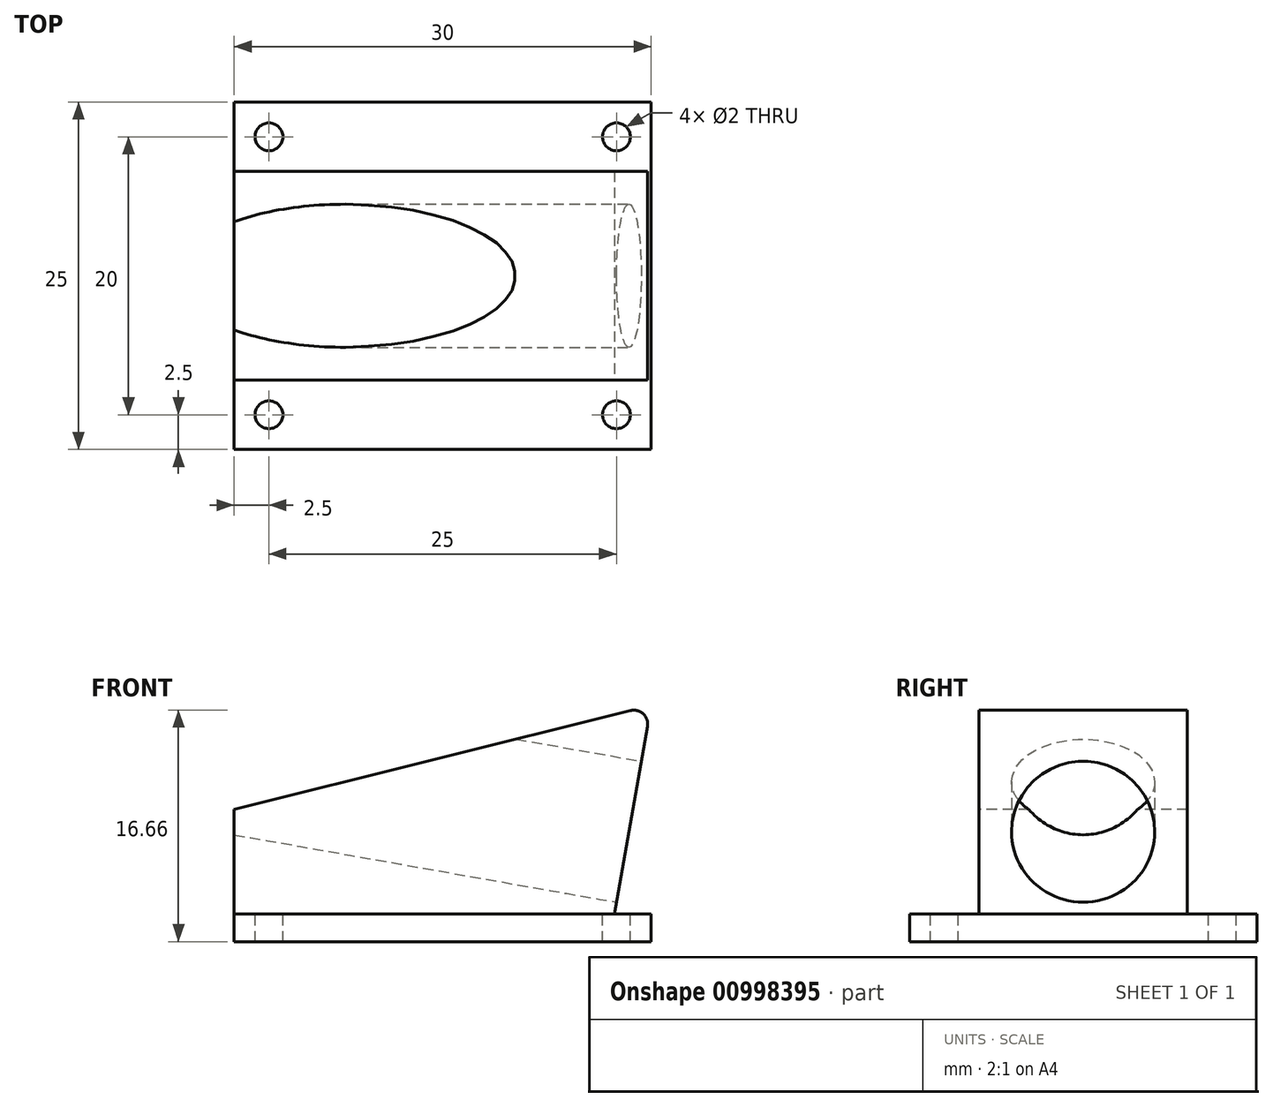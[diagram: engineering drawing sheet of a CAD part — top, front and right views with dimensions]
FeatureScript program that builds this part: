
annotation { "Feature Type Name" : "Feature", "Feature Type Description" : "" }
export const myFeature = defineFeature(function(context is Context, id is Id, definition is map)
    precondition{}
    {
        {
            var Q0;
            Q0=qCreatedBy(makeId("Top.planeOp"),FACE);
            var sketch = newSketch(context, id + "F0", { "sketchPlane" : qUnion([Q0])});
            skLineSegment(sketch, "E0.bottom", {"start": v(-15, 12.5) * mm, "end": v(15, 12.5) * mm});
            skLineSegment(sketch, "E0.top", {"start": v(-15, -12.5) * mm, "end": v(15, -12.5) * mm});
            skLineSegment(sketch, "E0.left", {"start": v(-15, 12.5) * mm, "end": v(-15, -12.5) * mm});
            skLineSegment(sketch, "E0.right", {"start": v(15, 12.5) * mm, "end": v(15, -12.5) * mm});
            skSolve(sketch);
        }
        {
            var Q0;
            Q0=makeQuery(id+"F0.imprint","IMPRINT",FACE,{"disambiguationData":[TD([[makeQuery(id+"F0.imprint","IMPRINT",EDGE,{"derivedFrom":sQuery(id+"F0.wireOp",EDGE,"E0.bottom")}),-1.0]])]});
            extrude(context, id + "F1", {"entities" : qUnion([Q0]), "depth" : 2 * mm, "offsetDistance" : 25 * mm});
        }
        {
            var Q0;
            Q0=makeQuery(id+"F1.opExtrude","CAP_FACE",FACE,{"disambiguationData":[OSD([sQuery(id+"F0.wireOp",EDGE,"E0.bottom"),sQuery(id+"F0.wireOp",EDGE,"E0.top"),sQuery(id+"F0.wireOp",EDGE,"E0.left"),sQuery(id+"F0.wireOp",EDGE,"E0.right")])],"isStart":false});
            var sketch = newSketch(context, id + "F2", { "sketchPlane" : qUnion([Q0])});
            skCircle(sketch, "E1", {"center": v(-12.5, 10) * mm, "radius": 1 * mm});
            skCircle(sketch, "E2", {"center": v(12.5, 10) * mm, "radius": 1 * mm});
            skCircle(sketch, "E3", {"center": v(12.5, -10) * mm, "radius": 1 * mm});
            skCircle(sketch, "E4", {"center": v(-12.5, -10) * mm, "radius": 1 * mm});
            skSolve(sketch);
        }
        {
            var Q0;
            Q0=makeQuery(id+"F2.imprint","IMPRINT",FACE,{"disambiguationData":[TD([[makeQuery(id+"F2.imprint","IMPRINT",EDGE,{"derivedFrom":sQuery(id+"F2.wireOp",EDGE,"E2")}),1.0]])]});
            var Q1;
            Q1=makeQuery(id+"F2.imprint","IMPRINT",FACE,{"disambiguationData":[TD([[makeQuery(id+"F2.imprint","IMPRINT",EDGE,{"derivedFrom":sQuery(id+"F2.wireOp",EDGE,"E1")}),1.0]])]});
            var Q2;
            Q2=makeQuery(id+"F2.imprint","IMPRINT",FACE,{"disambiguationData":[TD([[makeQuery(id+"F2.imprint","IMPRINT",EDGE,{"derivedFrom":sQuery(id+"F2.wireOp",EDGE,"E4")}),1.0]])]});
            var Q3;
            Q3=makeQuery(id+"F2.imprint","IMPRINT",FACE,{"disambiguationData":[TD([[makeQuery(id+"F2.imprint","IMPRINT",EDGE,{"derivedFrom":sQuery(id+"F2.wireOp",EDGE,"E3")}),1.0]])]});
            extrude(context, id + "F3", {"entities" : qUnion([Q0, Q1, Q2, Q3]), "operationType" : NewBodyOperationType.REMOVE, "oppositeDirection" : true, "depth" : 2 * mm, "offsetDistance" : 25 * mm});
        }
        {
            var Q0;
            Q0=makeQuery(id+"F1.opExtrude","CAP_FACE",FACE,{"disambiguationData":[OSD([sQuery(id+"F0.wireOp",EDGE,"E0.bottom"),sQuery(id+"F0.wireOp",EDGE,"E0.top"),sQuery(id+"F0.wireOp",EDGE,"E0.left"),sQuery(id+"F0.wireOp",EDGE,"E0.right")])],"isStart":false});
            var sketch = newSketch(context, id + "F4", { "sketchPlane" : qUnion([Q0])});
            skLineSegment(sketch, "E5.bottom", {"start": v(15, 7.5) * mm, "end": v(-15, 7.5) * mm});
            skLineSegment(sketch, "E5.top", {"start": v(15, -7.5) * mm, "end": v(-15, -7.5) * mm});
            skLineSegment(sketch, "E5.left", {"start": v(15, 7.5) * mm, "end": v(15, -7.5) * mm});
            skLineSegment(sketch, "E5.right", {"start": v(-15, 7.5) * mm, "end": v(-15, -7.5) * mm});
            skSolve(sketch);
        }
        {
            var Q0;
            Q0=makeQuery(id+"F4.imprint","IMPRINT",FACE,{"disambiguationData":[TD([[makeQuery(id+"F4.imprint","IMPRINT",EDGE,{"derivedFrom":sQuery(id+"F4.wireOp",EDGE,"E5.bottom")}),1.0]])]});
            extrude(context, id + "F5", {"entities" : qUnion([Q0]), "operationType" : NewBodyOperationType.ADD, "depth" : 15 * mm, "offsetDistance" : 25 * mm});
        }
        {
            var Q0;
            Q0=makeQuery(id+"F5.opExtrude","SWEPT_FACE",FACE,{"disambiguationData":[OSD([sQuery(id+"F4.wireOp",EDGE,"E5.top")])]});
            var sketch = newSketch(context, id + "F6", { "sketchPlane" : qUnion([Q0])});
            skLineSegment(sketch, "E6", {"start": v(15, 17) * mm, "end": v(-15, 2) * mm});
            skLineSegment(sketch, "E7", {"start": v(-15, 2) * mm, "end": v(-15, 17) * mm});
            skLineSegment(sketch, "E8", {"start": v(-15, 17) * mm, "end": v(15, 17) * mm});
            skLineSegment(sketch, "E9", {"start": v(15, 17) * mm, "end": v(-15, 9.5) * mm});
            skSolve(sketch);
        }
        {
            var Q0;
            {var subQ0=sQuery(id+"F6.wireOp",EDGE,"E8");Q0=makeQuery(id+"F6.imprint","IMPRINT",FACE,{"disambiguationData":[TD([[makeQuery(id+"F6.imprint","IMPRINT",EDGE,{"derivedFrom":subQ0}),1.0]])]});}
            extrude(context, id + "F7", {"entities" : qUnion([Q0]), "operationType" : NewBodyOperationType.REMOVE, "endBound" : BoundingType.UP_TO_NEXT, "oppositeDirection" : true, "depth" : 23 * mm, "offsetDistance" : 25 * mm});
        }
        {
            var Q0;
            Q0=makeQuery(id+"F5.opExtrude","SWEPT_FACE",FACE,{"disambiguationData":[OSD([sQuery(id+"F4.wireOp",EDGE,"E5.top")])]});
            var sketch = newSketch(context, id + "F8", { "sketchPlane" : qUnion([Q0])});
            skLineSegment(sketch, "E10", {"start": v(15, 17) * mm, "end": v(12.36, 2) * mm});
            skLineSegment(sketch, "E11", {"start": v(12.36, 2) * mm, "end": v(15, 2) * mm});
            skLineSegment(sketch, "E12", {"start": v(15, 2) * mm, "end": v(15, 17) * mm});
            skSolve(sketch);
        }
        {
            var Q0;
            Q0=makeQuery(id+"F8.imprint","IMPRINT",FACE,{"disambiguationData":[TD([[makeQuery(id+"F8.imprint","IMPRINT",EDGE,{"derivedFrom":sQuery(id+"F8.wireOp",EDGE,"E10")}),1.0]])]});
            extrude(context, id + "F9", {"entities" : qUnion([Q0]), "operationType" : NewBodyOperationType.REMOVE, "endBound" : BoundingType.UP_TO_NEXT, "oppositeDirection" : true, "depth" : 25 * mm, "offsetDistance" : 25 * mm});
        }
        {
            var Q0;
            Q0=makeQuery(id+"F9.boolean.opBoolean","COPY",FACE,{"derivedFrom":makeQuery(id+"F9.opExtrude","SWEPT_FACE",FACE,{"disambiguationData":[OSD([sQuery(id+"F8.wireOp",EDGE,"E10")])]})});
            var sketch = newSketch(context, id + "F10", { "sketchPlane" : qUnion([Q0])});
            skCircle(sketch, "E13", {"center": v(0, 10.12) * mm, "radius": 5.15 * mm});
            skSolve(sketch);
        }
        {
            var Q0;
            Q0=makeQuery(id+"F10.imprint","IMPRINT",FACE,{"disambiguationData":[TD([[makeQuery(id+"F10.imprint","IMPRINT",EDGE,{"derivedFrom":sQuery(id+"F10.wireOp",EDGE,"E13")}),1.0]])]});
            extrude(context, id + "F11", {"entities" : qUnion([Q0]), "operationType" : NewBodyOperationType.REMOVE, "endBound" : BoundingType.UP_TO_NEXT, "oppositeDirection" : true, "depth" : 25 * mm, "offsetDistance" : 25 * mm});
        }
        {
            var Q0;
            Q0=makeQuery(id+"F7.boolean.opBoolean","COPY",EDGE,{"derivedFrom":makeQuery(id+"F7.opExtrude","CAP_EDGE",EDGE,{"disambiguationData":[OSD([sQuery(id+"F6.wireOp",EDGE,"E6")])],"isStart":true})});
            var Q1;
            Q1=makeQuery(id+"F9.boolean.opBoolean","COPY",EDGE,{"derivedFrom":makeQuery(id+"F9.opExtrude","CAP_EDGE",EDGE,{"disambiguationData":[OSD([sQuery(id+"F8.wireOp",EDGE,"E10")])],"isStart":true})});
            var Q2;
            Q2=makeQuery(id+"F9.boolean.opBoolean","COPY",EDGE,{"derivedFrom":makeQuery(id+"F9.opExtrude","TWEAK_EDGE",EDGE,{"derivedFrom":[makeQuery(id+"F5.opExtrude","SWEPT_FACE",FACE,{"disambiguationData":[OSD([sQuery(id+"F4.wireOp",EDGE,"E5.bottom")])]}),makeQuery(id+"F8.imprint","IMPRINT",EDGE,{"derivedFrom":sQuery(id+"F8.wireOp",EDGE,"E10")})]})});
            var Q3;
            Q3=makeQuery(id+"F7.boolean.opBoolean","INTERSECT",EDGE,{"derivedFrom":[makeQuery(id+"F5.opExtrude","SWEPT_FACE",FACE,{"disambiguationData":[OSD([sQuery(id+"F4.wireOp",EDGE,"E5.bottom")])]}),makeQuery(id+"F7.opExtrude","SWEPT_FACE",FACE,{"disambiguationData":[OSD([sQuery(id+"F6.wireOp",EDGE,"E6")])]})]});
            var Q4;
            {var subQ0=sQuery(id+"F4.wireOp",EDGE,"E5.left");var subQ1=sQuery(id+"F4.wireOp",EDGE,"E5.bottom");var subQ2=sQuery(id+"F0.wireOp",EDGE,"E0.right");Q4=makeQuery(id+"F9.boolean.opBoolean","MERGE",EDGE,{"derivedFrom":[makeQuery(id+"F7.boolean.opBoolean","MERGE",EDGE,{"derivedFrom":[makeQuery(id+"F5.opExtrude","CAP_EDGE",EDGE,{"disambiguationData":[OSD([subQ0])],"isStart":false})],"fromTools":[makeQuery(id+"F7.opExtrude","SWEPT_EDGE",EDGE,{"disambiguationData":[OSD([subQ2,subQ1,subQ0])]})]})],"fromTools":[makeQuery(id+"F9.opExtrude","SWEPT_EDGE",EDGE,{"disambiguationData":[OSD([subQ2,subQ1,subQ0]),TDD([makeQuery(id+"F7.boolean.opBoolean","MERGE",VERTEX,{"derivedFrom":[makeQuery(id+"F5.opExtrude","CAP_VERTEX",VERTEX,{"disambiguationData":[OSD([subQ2,subQ1,subQ0])],"isStart":false})],"fromTools":[makeQuery(id+"F7.opExtrude","CAP_VERTEX",VERTEX,{"disambiguationData":[OSD([subQ2,subQ1,subQ0])],"isStart":false})]})])]})]});}
            fillet(context, id + "F12", {"entities" : qUnion([Q0, Q1, Q2, Q3, Q4]), "radius" : 1 * mm, "tangentPropagation" : true, "allowEdgeOverflow" : false});
        }
    });
